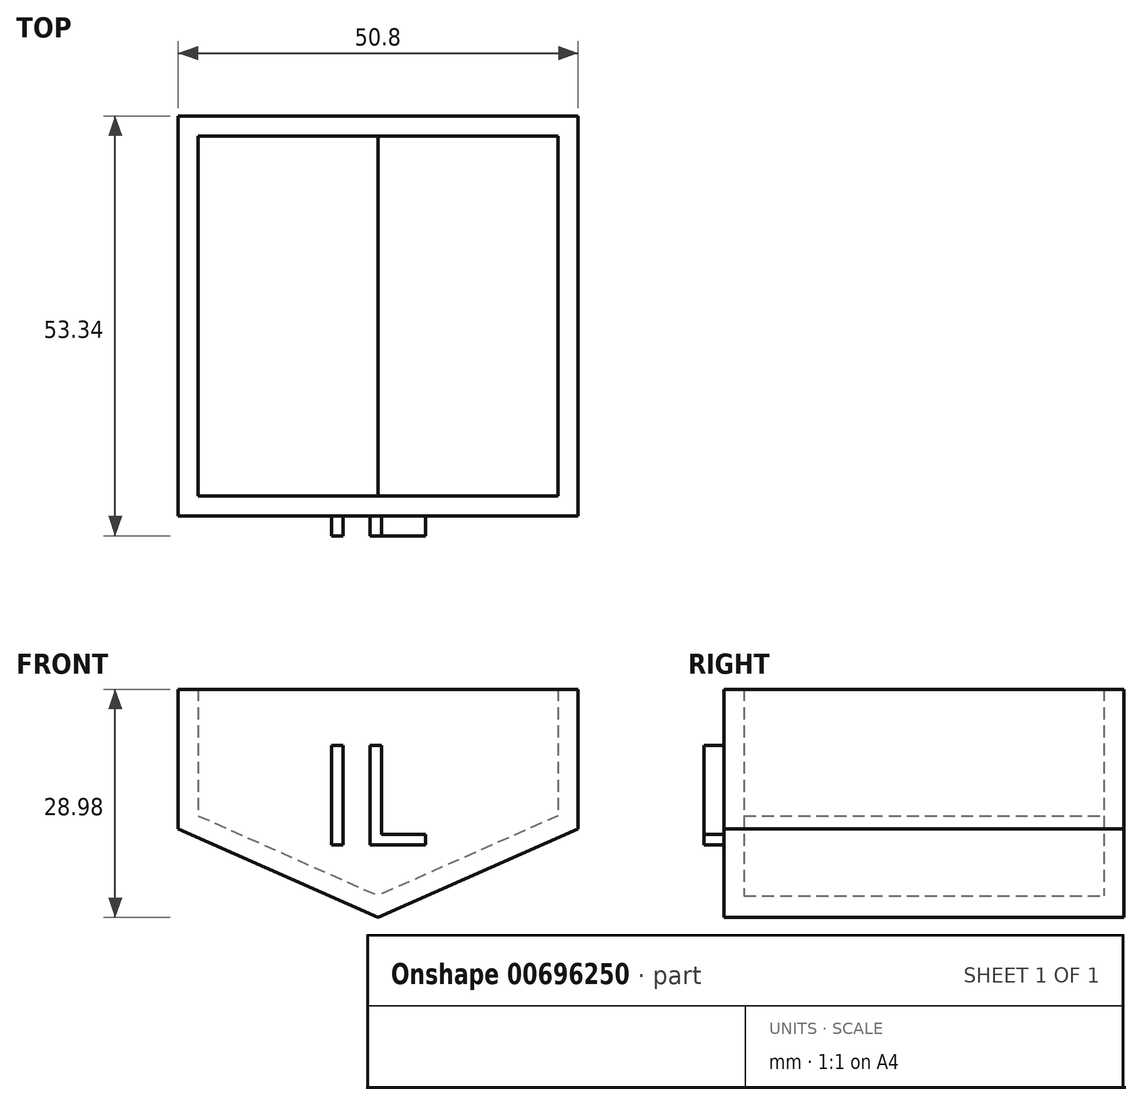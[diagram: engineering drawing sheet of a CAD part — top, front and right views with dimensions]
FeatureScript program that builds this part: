
annotation { "Feature Type Name" : "Feature", "Feature Type Description" : "" }
export const myFeature = defineFeature(function(context is Context, id is Id, definition is map)
    precondition{}
    {
        {
            var Q0;
            Q0=qCreatedBy(makeId("Front.planeOp"),FACE);
            var sketch = newSketch(context, id + "F0", { "sketchPlane" : qUnion([Q0])});
            skLineSegment(sketch, "E0", {"start": v(-25.36, 14.53) * mm, "end": v(25.44, 14.53) * mm});
            skLineSegment(sketch, "E1", {"start": v(25.44, 14.53) * mm, "end": v(25.44, -3.17) * mm});
            skLineSegment(sketch, "E2", {"start": v(25.44, -3.17) * mm, "end": v(0, -14.45) * mm});
            skLineSegment(sketch, "E3", {"start": v(-25.36, 14.53) * mm, "end": v(-25.36, -3.17) * mm});
            skLineSegment(sketch, "E4", {"start": v(-25.36, -3.17) * mm, "end": v(0, -14.45) * mm});
            skSolve(sketch);
        }
        {
            var Q0;
            Q0=makeQuery(id+"F0.imprint","IMPRINT",FACE,{"disambiguationData":[TD([[makeQuery(id+"F0.imprint","IMPRINT",EDGE,{"derivedFrom":sQuery(id+"F0.wireOp",EDGE,"E0")}),-1.0]])]});
            extrude(context, id + "F1", {"entities" : qUnion([Q0]), "depth" : 50.8 * mm, "offsetDistance" : 25.4 * mm});
        }
        {
            var Q0;
            Q0=makeQuery(id+"F1.opExtrude","SWEPT_FACE",FACE,{"disambiguationData":[OSD([sQuery(id+"F0.wireOp",EDGE,"E0")])]});
            shell(context, id + "F2", {"entities" : qUnion([Q0]), "thickness" : 2.54 * mm});
        }
        {
            var Q0;
            Q0=makeQuery(id+"F1.opExtrude","CAP_FACE",FACE,{"disambiguationData":[OSD([sQuery(id+"F0.wireOp",EDGE,"E0"),sQuery(id+"F0.wireOp",EDGE,"E1"),sQuery(id+"F0.wireOp",EDGE,"E2"),sQuery(id+"F0.wireOp",EDGE,"E3"),sQuery(id+"F0.wireOp",EDGE,"E4")])],"isStart":false});
            var sketch = newSketch(context, id + "F3", { "sketchPlane" : qUnion([Q0])});
            skText(sketch, "E5", { "text": "IL", "fontName": "OpenSans-Regular.ttf"});
            const initialGuessF3  = {"E5": [-0.00765, -0.00523, 1, 0, 0.01274]};
            skSetInitialGuess(sketch, initialGuessF3);
            skSolve(sketch);
        }
        {
            var Q0;
            Q0 = qSketchRegion(id + "F3", true);
            extrude(context, id + "F4", {"entities" : qUnion([Q0]), "operationType" : NewBodyOperationType.ADD, "depth" : 2.54 * mm, "offsetDistance" : 25.4 * mm});
        }
    });
